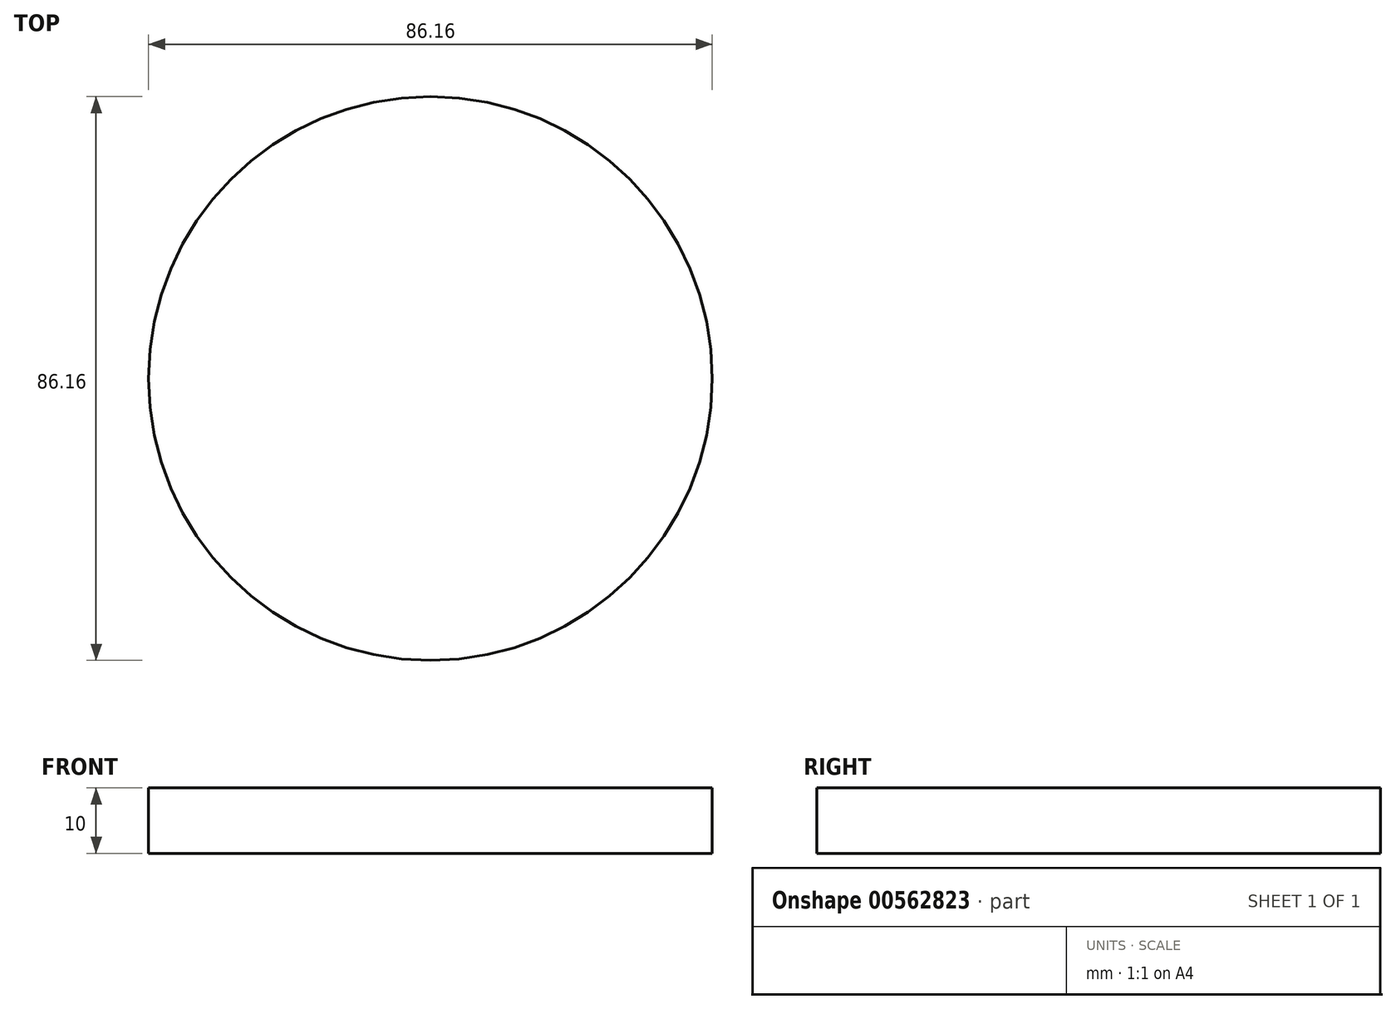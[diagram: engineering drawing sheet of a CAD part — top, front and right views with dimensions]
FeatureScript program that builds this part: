
annotation { "Feature Type Name" : "Feature", "Feature Type Description" : "" }
export const myFeature = defineFeature(function(context is Context, id is Id, definition is map)
    precondition{}
    {
        {
            var Q0;
            Q0=qCreatedBy(makeId("Top.planeOp"),FACE);
            var sketch = newSketch(context, id + "F0", { "sketchPlane" : qUnion([Q0])});
            skCircle(sketch, "E0", {"center": v(0, 0) * mm, "radius": 43.08 * mm});
            skSolve(sketch);
        }
        {
            var Q0;
            Q0=sQuery(id+"F0.wireOp",EDGE,"E0");
            extrude(context, id + "F1", {"bodyType" : ToolBodyType.SURFACE, "surfaceEntities" : qUnion([Q0]), "depth" : 10 * mm, "offsetDistance" : 25.4 * mm});
        }
    });
